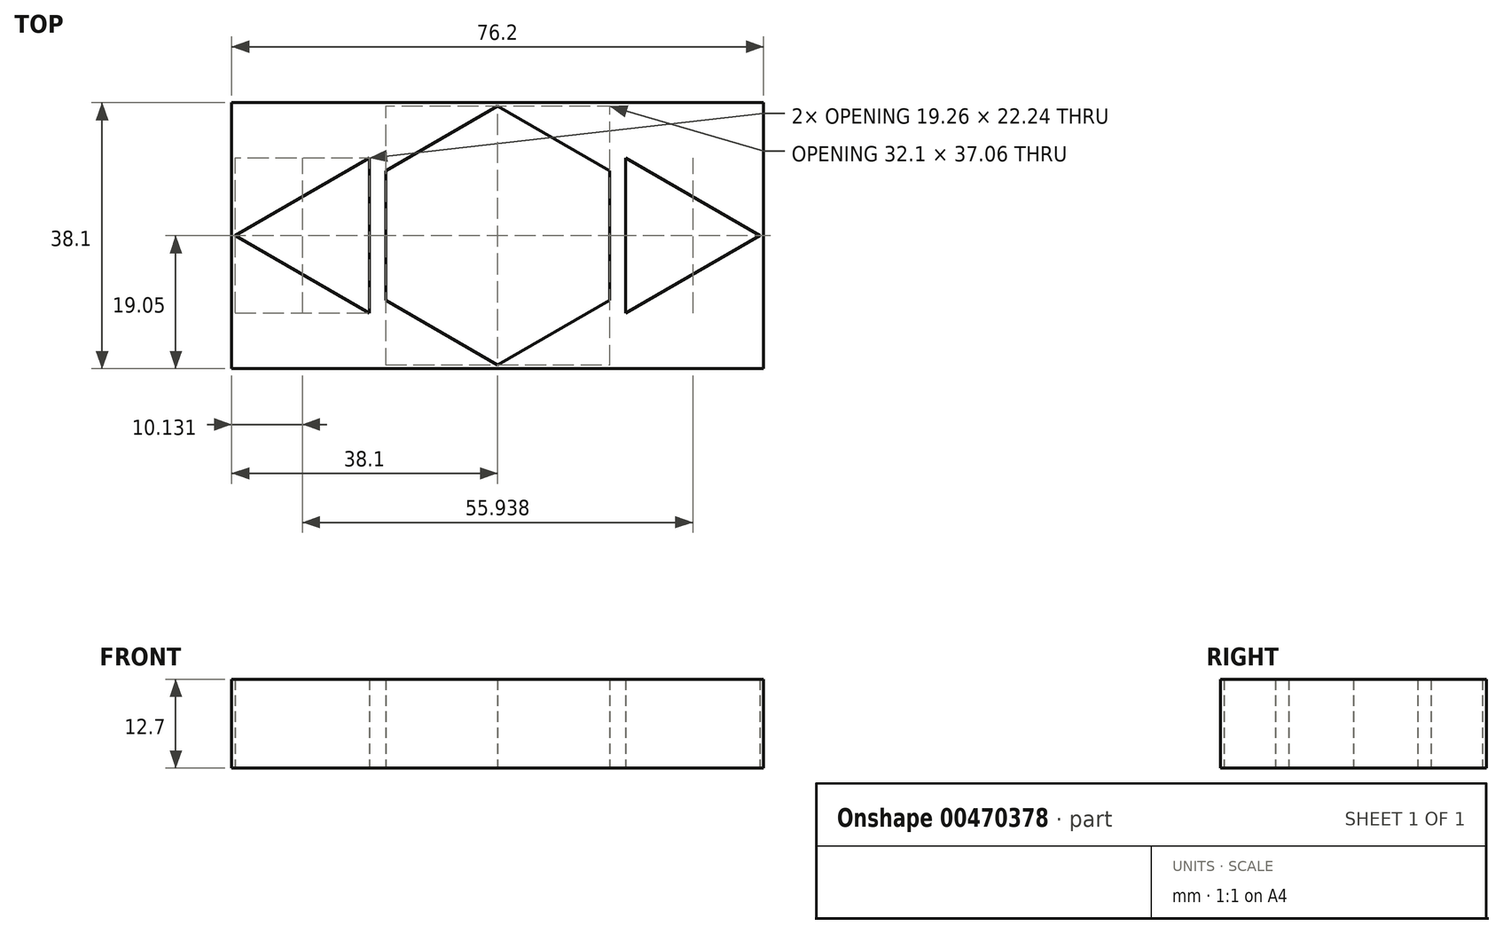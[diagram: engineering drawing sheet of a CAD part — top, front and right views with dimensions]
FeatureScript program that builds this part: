
annotation { "Feature Type Name" : "Feature", "Feature Type Description" : "" }
export const myFeature = defineFeature(function(context is Context, id is Id, definition is map)
    precondition{}
    {
        {
            var Q0;
            Q0=qCreatedBy(makeId("Top.planeOp"),FACE);
            var sketch = newSketch(context, id + "F0", { "sketchPlane" : qUnion([Q0])});
            skLineSegment(sketch, "E0.bottom", {"start": v(-38.1, 19.05) * mm, "end": v(38.1, 19.05) * mm});
            skLineSegment(sketch, "E0.top", {"start": v(-38.1, -19.05) * mm, "end": v(38.1, -19.05) * mm});
            skLineSegment(sketch, "E0.left", {"start": v(-38.1, 19.05) * mm, "end": v(-38.1, -19.05) * mm});
            skLineSegment(sketch, "E0.right", {"start": v(38.1, 19.05) * mm, "end": v(38.1, -19.05) * mm});
            skPoint(sketch, "E0.middle", {"position": v(0, 0) * mm});
            skCircle(sketch, "E1.cCircle", {"center": v(0, 0) * mm, "radius": 16.05 * mm, "construction": true});
            skLineSegment(sketch, "E1.0", {"start": v(-16.05, -9.27) * mm, "end": v(-16.05, 9.27) * mm});
            skLineSegment(sketch, "E1.1", {"start": v(-16.05, 9.27) * mm, "end": v(0, 18.53) * mm});
            skLineSegment(sketch, "E1.2", {"start": v(0, 18.53) * mm, "end": v(16.05, 9.27) * mm});
            skLineSegment(sketch, "E1.3", {"start": v(16.05, 9.27) * mm, "end": v(16.05, -9.27) * mm});
            skLineSegment(sketch, "E1.4", {"start": v(16.05, -9.27) * mm, "end": v(0, -18.53) * mm});
            skLineSegment(sketch, "E1.5", {"start": v(0, -18.53) * mm, "end": v(-16.05, -9.27) * mm});
            skPoint(sketch, "E1.0.midPoint", {"position": v(-16.05, 0) * mm});
            skCircle(sketch, "E2.cCircle", {"center": v(-24.76, 0) * mm, "radius": 6.42 * mm, "construction": true});
            skLineSegment(sketch, "E2.0", {"start": v(-18.34, 11.12) * mm, "end": v(-18.34, -11.12) * mm});
            skLineSegment(sketch, "E2.1", {"start": v(-18.34, -11.12) * mm, "end": v(-37.6, 0) * mm});
            skLineSegment(sketch, "E2.2", {"start": v(-37.6, 0) * mm, "end": v(-18.34, 11.12) * mm});
            skPoint(sketch, "E2.0.midPoint", {"position": v(-18.34, 0) * mm});
            skCircle(sketch, "E3.cCircle", {"center": v(24.76, 0) * mm, "radius": 6.42 * mm, "construction": true});
            skLineSegment(sketch, "E3.0", {"start": v(18.34, -11.12) * mm, "end": v(18.34, 11.12) * mm});
            skLineSegment(sketch, "E3.1", {"start": v(18.34, 11.12) * mm, "end": v(37.6, 0) * mm});
            skLineSegment(sketch, "E3.2", {"start": v(37.6, 0) * mm, "end": v(18.34, -11.12) * mm});
            skPoint(sketch, "E3.0.midPoint", {"position": v(18.34, 0) * mm});
            skSolve(sketch);
        }
        {
            var Q0;
            Q0 = qSketchRegion(id + "F0", true);
            extrude(context, id + "F1", {"entities" : qUnion([Q0]), "depth" : 12.7 * mm});
        }
    });
